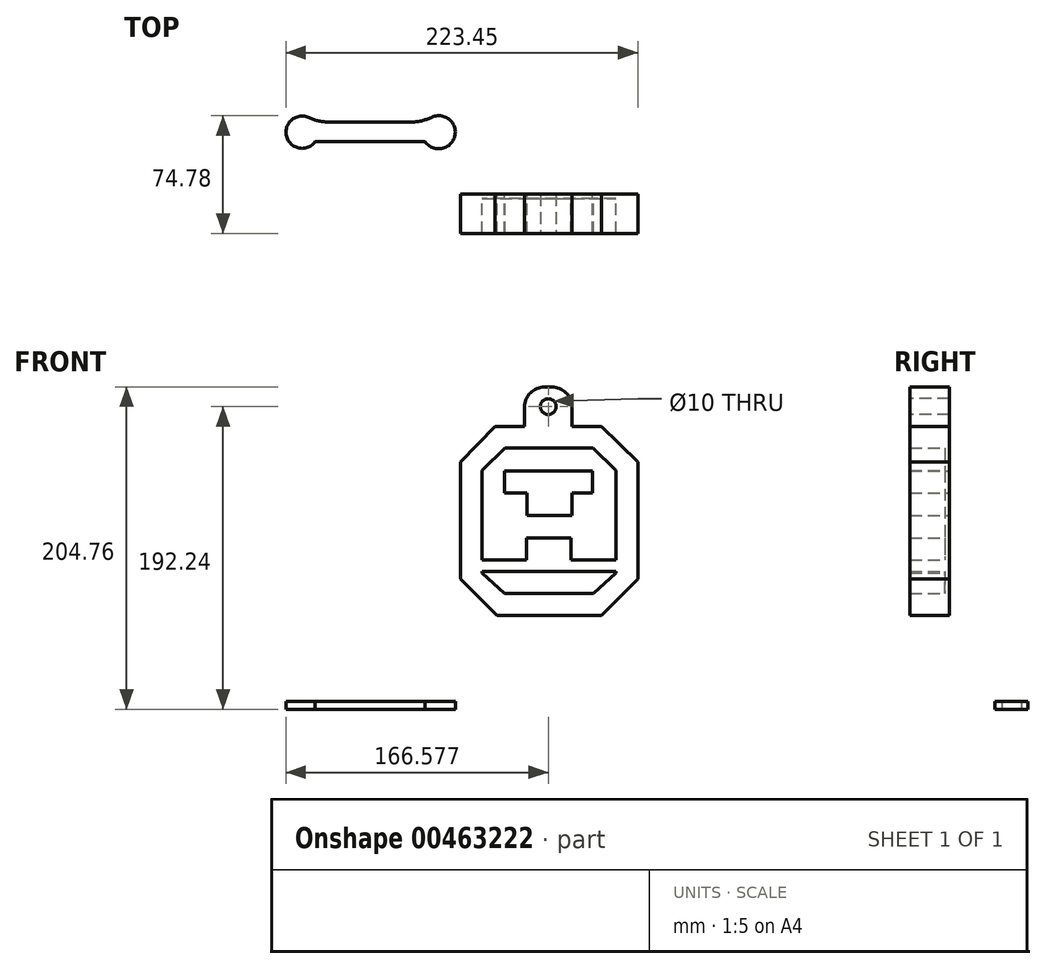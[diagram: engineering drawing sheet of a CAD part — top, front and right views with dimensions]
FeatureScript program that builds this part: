
annotation { "Feature Type Name" : "Feature", "Feature Type Description" : "" }
export const myFeature = defineFeature(function(context is Context, id is Id, definition is map)
    precondition{}
    {
        {
            var Q0;
            Q0=qCreatedBy(makeId("Top.planeOp"),FACE);
            var sketch = newSketch(context, id + "F0", { "sketchPlane" : qUnion([Q0])});
            skLineSegment(sketch, "E0", {"start": v(-45.32, -18.98) * mm, "end": v(14.68, -18.98) * mm});
            skLineSegment(sketch, "E1", {"start": v(-45.32, -18.98) * mm, "end": v(-45.32, -10.98) * mm});
            skLineSegment(sketch, "E2", {"start": v(-45.32, -10.98) * mm, "end": v(14.68, -10.98) * mm});
            skLineSegment(sketch, "E3", {"start": v(-70.25, -14.98) * mm, "end": v(54.87, -14.98) * mm});
            skPoint(sketch, "E3.startSnap0", {"position": v(-45.32, -14.98) * mm});
            skLineSegment(sketch, "E4", {"start": v(54.87, -14.98) * mm, "end": v(51.87, -14.98) * mm});
            skLineSegment(sketch, "E5", {"start": v(51.87, -14.98) * mm, "end": v(47.87, -14.98) * mm});
            skArc(sketch, "E6", {"start": v(-41.83, 45.67) * mm, "mid": v(-60.11, 39) * mm, "end": v(-41.53, 33.25) * mm});
            skArc(sketch, "E7", {"start": v(28.25, 33.25) * mm, "mid": v(47.4, 39.01) * mm, "end": v(28.54, 45.67) * mm});
            skLineSegment(sketch, "E8", {"start": v(-41.83, 45.67) * mm, "end": v(28.54, 45.67) * mm});
            skLineSegment(sketch, "E9", {"start": v(-41.53, 33.25) * mm, "end": v(28.25, 33.25) * mm});
            skSolve(sketch);
        }
        {
            var Q0;
            Q0 = qSketchRegion(id + "F0", true);
            extrude(context, id + "F1", {"entities" : qUnion([Q0]), "depth" : 5 * mm});
        }
        {
            var Q0;
            Q0=makeQuery(id+"F1.opExtrude","SWEPT_EDGE",EDGE,{"disambiguationData":[OSD([sQuery(id+"F0.wireOp",EDGE,"E6"),sQuery(id+"F0.wireOp",EDGE,"E8")])]});
            var Q1;
            Q1=makeQuery(id+"F1.opExtrude","SWEPT_EDGE",EDGE,{"disambiguationData":[OSD([sQuery(id+"F0.wireOp",EDGE,"E7"),sQuery(id+"F0.wireOp",EDGE,"E8")])]});
            fillet(context, id + "F2", {"entities" : qUnion([Q0, Q1]), "radius" : 30 * mm, "tangentPropagation" : true, "allowEdgeOverflow" : false});
        }
        {
            var Q0;
            Q0=qCreatedBy(makeId("Front.planeOp"),FACE);
            var sketch = newSketch(context, id + "F3", { "sketchPlane" : qUnion([Q0])});
            skLineSegment(sketch, "E10", {"start": v(50.79, 157.2) * mm, "end": v(50.79, 82.84) * mm});
            skLineSegment(sketch, "E11", {"start": v(50.79, 157.2) * mm, "end": v(181.88, 157.2) * mm, "construction": true});
            skLineSegment(sketch, "E12", {"start": v(181.88, 157.2) * mm, "end": v(181.88, 82.84) * mm, "construction": true});
            skLineSegment(sketch, "E13", {"start": v(181.88, 82.84) * mm, "end": v(50.79, 82.84) * mm, "construction": true});
            skLineSegment(sketch, "E14", {"start": v(74.63, 179.76) * mm, "end": v(140.18, 179.76) * mm});
            skLineSegment(sketch, "E15", {"start": v(163.33, 157.2) * mm, "end": v(163.33, 82.84) * mm});
            skLineSegment(sketch, "E16", {"start": v(64.4, 151.54) * mm, "end": v(64.4, 94.98) * mm});
            skLineSegment(sketch, "E17", {"start": v(64.4, 94.98) * mm, "end": v(92.61, 94.98) * mm});
            skLineSegment(sketch, "E18", {"start": v(92.61, 94.98) * mm, "end": v(92.61, 108.68) * mm});
            skLineSegment(sketch, "E19", {"start": v(92.61, 108.68) * mm, "end": v(120.81, 108.68) * mm});
            skLineSegment(sketch, "E20", {"start": v(120.81, 108.68) * mm, "end": v(120.81, 94.98) * mm});
            skLineSegment(sketch, "E21", {"start": v(120.81, 94.98) * mm, "end": v(149.36, 94.98) * mm});
            skLineSegment(sketch, "E22", {"start": v(149.36, 94.98) * mm, "end": v(149.36, 151.54) * mm});
            skLineSegment(sketch, "E23", {"start": v(149.36, 151.54) * mm, "end": v(134.97, 165.88) * mm});
            skLineSegment(sketch, "E24", {"start": v(134.97, 165.88) * mm, "end": v(78.92, 165.88) * mm});
            skLineSegment(sketch, "E25", {"start": v(78.92, 165.88) * mm, "end": v(64.4, 151.54) * mm});
            skLineSegment(sketch, "E26", {"start": v(64.4, 87.45) * mm, "end": v(149.53, 87.45) * mm});
            skLineSegment(sketch, "E27", {"start": v(149.53, 87.45) * mm, "end": v(149.53, 86.69) * mm});
            skLineSegment(sketch, "E28", {"start": v(149.53, 86.69) * mm, "end": v(135.2, 73.45) * mm});
            skLineSegment(sketch, "E29", {"start": v(135.2, 73.45) * mm, "end": v(78.56, 73.45) * mm});
            skLineSegment(sketch, "E30", {"start": v(78.56, 73.45) * mm, "end": v(64.4, 86.56) * mm});
            skLineSegment(sketch, "E31", {"start": v(64.4, 86.56) * mm, "end": v(64.4, 87.45) * mm});
            skLineSegment(sketch, "E32", {"start": v(50.79, 82.84) * mm, "end": v(73.75, 59.5) * mm});
            skLineSegment(sketch, "E33", {"start": v(73.75, 59.5) * mm, "end": v(140.12, 59.5) * mm});
            skLineSegment(sketch, "E34", {"start": v(140.12, 59.5) * mm, "end": v(163.33, 82.84) * mm});
            skLineSegment(sketch, "E35", {"start": v(78.71, 151.38) * mm, "end": v(78.71, 137.48) * mm});
            skLineSegment(sketch, "E36", {"start": v(78.71, 137.48) * mm, "end": v(93.03, 137.48) * mm});
            skLineSegment(sketch, "E37", {"start": v(93.03, 137.48) * mm, "end": v(93.03, 123.02) * mm});
            skLineSegment(sketch, "E38", {"start": v(93.03, 123.02) * mm, "end": v(121.4, 123.02) * mm});
            skLineSegment(sketch, "E39", {"start": v(121.4, 123.02) * mm, "end": v(121.4, 137.48) * mm});
            skLineSegment(sketch, "E40", {"start": v(121.4, 137.48) * mm, "end": v(134.58, 137.48) * mm});
            skLineSegment(sketch, "E41", {"start": v(134.58, 137.48) * mm, "end": v(134.58, 151.38) * mm});
            skLineSegment(sketch, "E42", {"start": v(134.58, 151.38) * mm, "end": v(78.71, 151.38) * mm});
            skLineSegment(sketch, "E43", {"start": v(106.65, 151.38) * mm, "end": v(106.65, 119.62) * mm});
            skLineSegment(sketch, "E44.MirrorCS", {"start": v(134.58, 151.38) * mm, "end": v(134.58, 137.48) * mm});
            skLineSegment(sketch, "E45.MirrorCS", {"start": v(134.58, 137.48) * mm, "end": v(121.4, 137.48) * mm});
            skLineSegment(sketch, "E46.MirrorCS", {"start": v(120.26, 123.02) * mm, "end": v(91.9, 123.02) * mm});
            skLineSegment(sketch, "E47.MirrorCS", {"start": v(78.71, 151.38) * mm, "end": v(134.58, 151.38) * mm});
            skPoint(sketch, "E48.MirrorCS.end.orphan", {"position": v(120.26, 123.02) * mm});
            skPoint(sketch, "E48.MirrorCS.start.orphan", {"position": v(120.26, 137.48) * mm});
            skLineSegment(sketch, "E49", {"start": v(50.79, 157.2) * mm, "end": v(72.74, 179.76) * mm});
            skLineSegment(sketch, "E50", {"start": v(74.63, 179.76) * mm, "end": v(72.74, 179.76) * mm});
            skLineSegment(sketch, "E51", {"start": v(140.18, 179.76) * mm, "end": v(163.33, 157.2) * mm});
            skSolve(sketch);
        }
        {
            var Q0;
            Q0=makeQuery(id+"F3.imprint","IMPRINT",FACE,{"disambiguationData":[TD([[makeQuery(id+"F3.imprint","IMPRINT",EDGE,{"derivedFrom":sQuery(id+"F3.wireOp",EDGE,"E10")}),1.0]])]});
            var Q1;
            {var subQ6=sQuery(id+"F3.wireOp",EDGE,"E35");Q1=makeQuery(id+"F3.imprint","IMPRINT",FACE,{"disambiguationData":[TD([[makeQuery(id+"F3.imprint","IMPRINT",EDGE,{"derivedFrom":subQ6}),1.0]])]});}
            var Q2;
            {var subQ5=sQuery(id+"F3.wireOp",EDGE,"E38");Q2=makeQuery(id+"F3.imprint","IMPRINT",FACE,{"disambiguationData":[TD([[makeQuery(id+"F3.imprint","IMPRINT",EDGE,{"derivedFrom":subQ5}),1.0]])]});}
            extrude(context, id + "F4", {"entities" : qUnion([Q0, Q1, Q2]), "depth" : 25 * mm, "offsetDistance" : 25 * mm});
        }
        {
            var Q0;
            Q0=makeQuery(id+"F3.imprint","IMPRINT",FACE,{"disambiguationData":[TD([[makeQuery(id+"F3.imprint","IMPRINT",EDGE,{"derivedFrom":sQuery(id+"F3.wireOp",EDGE,"E16")}),1.0]])]});
            var Q1;
            Q1=makeQuery(id+"F3.imprint","IMPRINT",FACE,{"disambiguationData":[TD([[makeQuery(id+"F3.imprint","IMPRINT",EDGE,{"derivedFrom":sQuery(id+"F3.wireOp",EDGE,"E10")}),1.0]])]});
            var Q2;
            {var subQ5=sQuery(id+"F3.wireOp",EDGE,"E38");Q2=makeQuery(id+"F3.imprint","IMPRINT",FACE,{"disambiguationData":[TD([[makeQuery(id+"F3.imprint","IMPRINT",EDGE,{"derivedFrom":subQ5}),1.0]])]});}
            var Q3;
            {var subQ6=sQuery(id+"F3.wireOp",EDGE,"E35");Q3=makeQuery(id+"F3.imprint","IMPRINT",FACE,{"disambiguationData":[TD([[makeQuery(id+"F3.imprint","IMPRINT",EDGE,{"derivedFrom":subQ6}),1.0]])]});}
            var Q4;
            Q4=makeQuery(id+"F3.imprint","IMPRINT",FACE,{"disambiguationData":[TD([[makeQuery(id+"F3.imprint","IMPRINT",EDGE,{"derivedFrom":sQuery(id+"F3.wireOp",EDGE,"E26")}),-1.0]])]});
            extrude(context, id + "F5", {"entities" : qUnion([Q0, Q1, Q2, Q3, Q4]), "depth" : 3 * mm, "offsetDistance" : 25 * mm});
        }
        {
            var Q0;
            Q0=makeQuery(id+"F4.opExtrude","SWEPT_FACE",FACE,{"disambiguationData":[OSD([sQuery(id+"F3.wireOp",EDGE,"E14"),sQuery(id+"F3.wireOp",EDGE,"E50")])]});
            var sketch = newSketch(context, id + "F6", { "sketchPlane" : qUnion([Q0])});
            skLineSegment(sketch, "E52", {"start": v(106.46, -25) * mm, "end": v(121.46, -25) * mm});
            skLineSegment(sketch, "E53.bottom", {"start": v(121.46, -25) * mm, "end": v(91.46, -25) * mm});
            skLineSegment(sketch, "E53.top", {"start": v(121.46, 0) * mm, "end": v(91.46, 0) * mm});
            skLineSegment(sketch, "E53.left", {"start": v(121.46, -25) * mm, "end": v(121.46, 0) * mm});
            skLineSegment(sketch, "E53.right", {"start": v(91.46, -25) * mm, "end": v(91.46, 0) * mm});
            skSolve(sketch);
        }
        {
            var Q0;
            Q0 = qSketchRegion(id + "F6", true);
            extrude(context, id + "F7", {"entities" : qUnion([Q0]), "operationType" : NewBodyOperationType.ADD, "depth" : 25 * mm, "offsetDistance" : 25 * mm});
        }
        {
            var Q0;
            Q0=makeQuery(id+"F7.opExtrude","CAP_EDGE",EDGE,{"disambiguationData":[OSD([sQuery(id+"F6.wireOp",EDGE,"E53.right")])],"isStart":false});
            var Q1;
            Q1=makeQuery(id+"F7.opExtrude","CAP_EDGE",EDGE,{"disambiguationData":[OSD([sQuery(id+"F6.wireOp",EDGE,"E53.left")])],"isStart":false});
            fillet(context, id + "F8", {"entities" : qUnion([Q0, Q1]), "tangentPropagation" : true, "radius" : 12.8 * mm, "defaultsChanged" : false, "vertexSettings" : [], "allowEdgeOverflow" : false});
        }
        {
            var Q0;
            Q0=makeQuery(id+"F7.boolean.opBoolean","MERGE",FACE,{"derivedFrom":[makeQuery(id+"F4.opExtrude","CAP_FACE",FACE,{"disambiguationData":[OSD([sQuery(id+"F3.wireOp",EDGE,"E10"),sQuery(id+"F3.wireOp",EDGE,"E14"),sQuery(id+"F3.wireOp",EDGE,"E15"),sQuery(id+"F3.wireOp",EDGE,"E16"),sQuery(id+"F3.wireOp",EDGE,"E17"),sQuery(id+"F3.wireOp",EDGE,"E18"),sQuery(id+"F3.wireOp",EDGE,"E19"),sQuery(id+"F3.wireOp",EDGE,"E20"),sQuery(id+"F3.wireOp",EDGE,"E21"),sQuery(id+"F3.wireOp",EDGE,"E22"),sQuery(id+"F3.wireOp",EDGE,"E23"),sQuery(id+"F3.wireOp",EDGE,"E24"),sQuery(id+"F3.wireOp",EDGE,"E25"),sQuery(id+"F3.wireOp",EDGE,"E26"),sQuery(id+"F3.wireOp",EDGE,"E27"),sQuery(id+"F3.wireOp",EDGE,"E28"),sQuery(id+"F3.wireOp",EDGE,"E29"),sQuery(id+"F3.wireOp",EDGE,"E30"),sQuery(id+"F3.wireOp",EDGE,"E31"),sQuery(id+"F3.wireOp",EDGE,"E32"),sQuery(id+"F3.wireOp",EDGE,"E33"),sQuery(id+"F3.wireOp",EDGE,"E34"),sQuery(id+"F3.wireOp",EDGE,"E49"),sQuery(id+"F3.wireOp",EDGE,"E50"),sQuery(id+"F3.wireOp",EDGE,"E51")])],"isStart":false}),makeQuery(id+"F7.opExtrude","SWEPT_FACE",FACE,{"disambiguationData":[OSD([sQuery(id+"F6.wireOp",EDGE,"E53.bottom")])]})]});
            var sketch = newSketch(context, id + "F9", { "sketchPlane" : qUnion([Q0])});
            skCircle(sketch, "E54", {"center": v(106.46, 192.24) * mm, "radius": 5 * mm});
            skPoint(sketch, "E55.start.orphan", {"position": v(106.46, 204.72) * mm});
            skPoint(sketch, "E56.trimOffspring.end.orphan", {"position": v(131.46, 179.76) * mm});
            skPoint(sketch, "E56.trimOffspring.start.orphan", {"position": v(118.96, 192.24) * mm});
            skPoint(sketch, "E57.end.orphan", {"position": v(93.96, 192.24) * mm});
            skPoint(sketch, "E57.start.orphan", {"position": v(81.46, 179.76) * mm});
            skSolve(sketch);
        }
        {
            var Q0;
            Q0=makeQuery(id+"F9.imprint","IMPRINT",FACE,{"disambiguationData":[TD([[makeQuery(id+"F9.imprint","IMPRINT",EDGE,{"derivedFrom":sQuery(id+"F9.wireOp",EDGE,"E54")}),1.0]])]});
            extrude(context, id + "F10", {"entities" : qUnion([Q0]), "operationType" : NewBodyOperationType.REMOVE, "oppositeDirection" : true, "depth" : 44.9 * mm, "offsetDistance" : 25 * mm});
        }
    });
